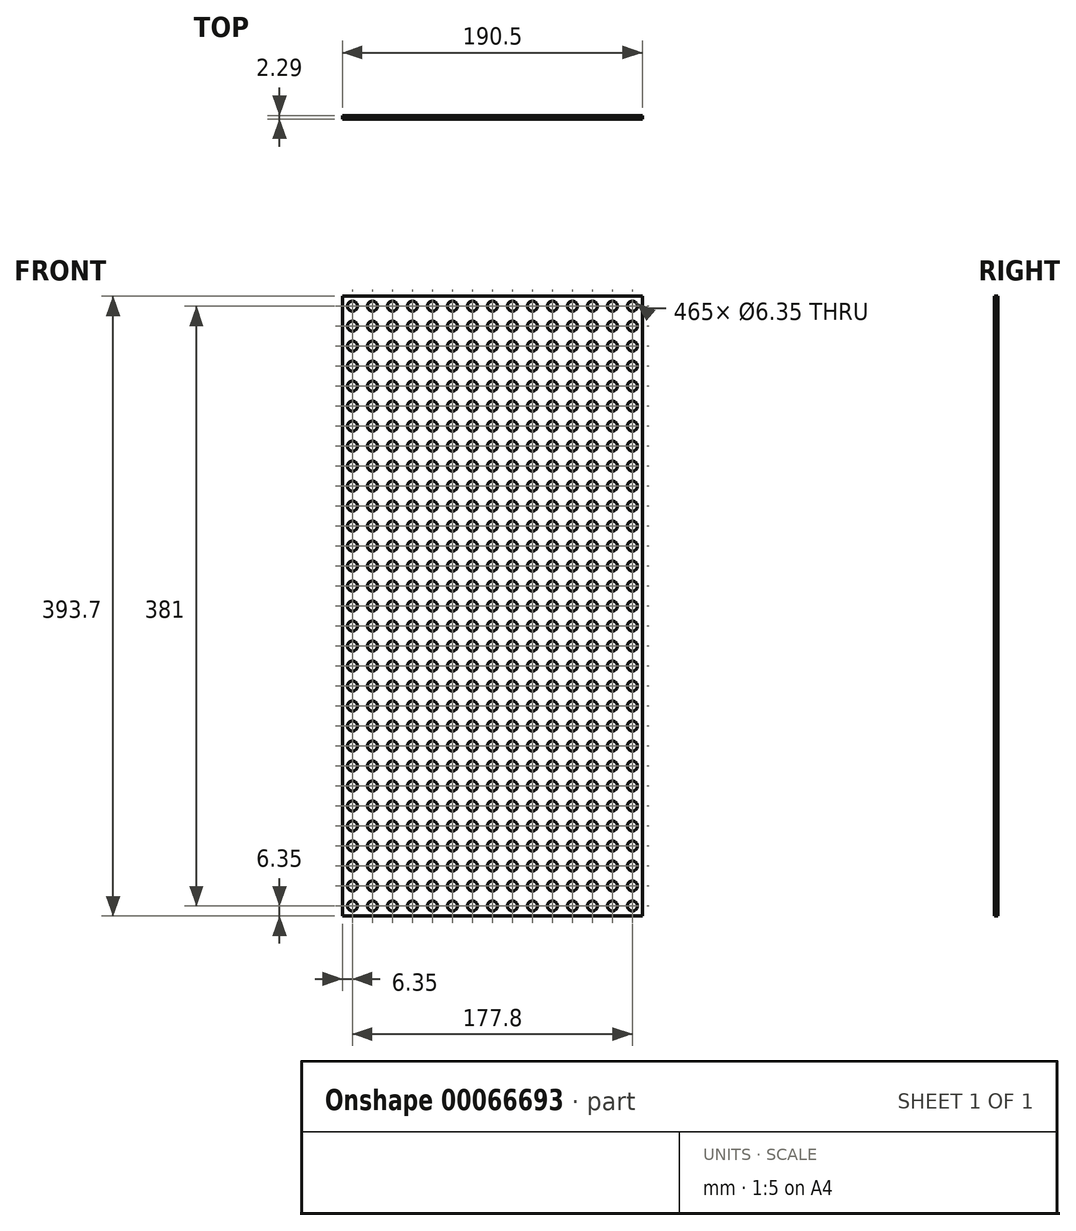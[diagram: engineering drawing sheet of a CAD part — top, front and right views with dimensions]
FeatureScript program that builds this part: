
annotation { "Feature Type Name" : "Feature", "Feature Type Description" : "" }
export const myFeature = defineFeature(function(context is Context, id is Id, definition is map)
    precondition{}
    {
        {
            var Q0;
            Q0=qCreatedBy(makeId("Front.planeOp"),FACE);
            var sketch = newSketch(context, id + "F0", { "sketchPlane" : qUnion([Q0])});
            skLineSegment(sketch, "E0.bottom", {"start": v(-95.25, 196.85) * mm, "end": v(95.25, 196.85) * mm});
            skLineSegment(sketch, "E0.top", {"start": v(-95.25, -196.85) * mm, "end": v(95.25, -196.85) * mm});
            skLineSegment(sketch, "E0.left", {"start": v(-95.25, 196.85) * mm, "end": v(-95.25, -196.85) * mm});
            skLineSegment(sketch, "E0.right", {"start": v(95.25, 196.85) * mm, "end": v(95.25, -196.85) * mm});
            skSolve(sketch);
        }
        {
            var Q0;
            Q0 = qSketchRegion(id + "F0", true);
            extrude(context, id + "F1", {"entities" : qUnion([Q0]), "depth" : 2.3 * mm});
        }
        {
            var Q0;
            Q0=makeQuery(id+"F1.opExtrude","CAP_FACE",FACE,{"disambiguationData":[OSD([sQuery(id+"F0.wireOp",EDGE,"E0.bottom"),sQuery(id+"F0.wireOp",EDGE,"E0.top"),sQuery(id+"F0.wireOp",EDGE,"E0.left"),sQuery(id+"F0.wireOp",EDGE,"E0.right")])],"isStart":false});
            var sketch = newSketch(context, id + "F2", { "sketchPlane" : qUnion([Q0])});
            skCircle(sketch, "E1", {"center": v(-88.9, 190.5) * mm, "radius": 3.18 * mm});
            skCircle(sketch, "E2.0.1.0", {"center": v(-88.9, 177.8) * mm, "radius": 3.18 * mm});
            skCircle(sketch, "E2.1.0.0", {"center": v(-76.2, 190.5) * mm, "radius": 3.18 * mm});
            skCircle(sketch, "E2.1.1.0", {"center": v(-76.2, 177.8) * mm, "radius": 3.18 * mm});
            skCircle(sketch, "E2.2.0.0", {"center": v(-63.5, 190.5) * mm, "radius": 3.18 * mm});
            skCircle(sketch, "E2.2.1.0", {"center": v(-63.5, 177.8) * mm, "radius": 3.18 * mm});
            skLineSegment(sketch, "E2.direction1", {"start": v(-88.9, 190.5) * mm, "end": v(-76.2, 190.5) * mm, "construction": true});
            skLineSegment(sketch, "E2.direction2", {"start": v(-88.9, 190.5) * mm, "end": v(-88.9, 177.8) * mm, "construction": true});
            skCircle(sketch, "E3.0.3.0", {"center": v(-50.8, 190.5) * mm, "radius": 3.18 * mm});
            skCircle(sketch, "E3.0.3.1", {"center": v(-50.8, 177.8) * mm, "radius": 3.18 * mm});
            skCircle(sketch, "E3.0.4.0", {"center": v(-38.1, 190.5) * mm, "radius": 3.18 * mm});
            skCircle(sketch, "E3.0.4.1", {"center": v(-38.1, 177.8) * mm, "radius": 3.18 * mm});
            skCircle(sketch, "E3.0.5.0", {"center": v(-25.4, 190.5) * mm, "radius": 3.18 * mm});
            skCircle(sketch, "E3.0.5.1", {"center": v(-25.4, 177.8) * mm, "radius": 3.18 * mm});
            skCircle(sketch, "E3.0.6.0", {"center": v(-12.7, 190.5) * mm, "radius": 3.18 * mm});
            skCircle(sketch, "E3.0.6.1", {"center": v(-12.7, 177.8) * mm, "radius": 3.18 * mm});
            skCircle(sketch, "E3.0.7.0", {"center": v(0, 190.5) * mm, "radius": 3.18 * mm});
            skCircle(sketch, "E3.0.7.1", {"center": v(0, 177.8) * mm, "radius": 3.18 * mm});
            skCircle(sketch, "E3.0.8.0", {"center": v(12.7, 190.5) * mm, "radius": 3.18 * mm});
            skCircle(sketch, "E3.0.8.1", {"center": v(12.7, 177.8) * mm, "radius": 3.18 * mm});
            skCircle(sketch, "E3.0.9.0", {"center": v(25.4, 190.5) * mm, "radius": 3.18 * mm});
            skCircle(sketch, "E3.0.9.1", {"center": v(25.4, 177.8) * mm, "radius": 3.18 * mm});
            skCircle(sketch, "E3.0.10.0", {"center": v(38.1, 190.5) * mm, "radius": 3.18 * mm});
            skCircle(sketch, "E3.0.10.1", {"center": v(38.1, 177.8) * mm, "radius": 3.18 * mm});
            skCircle(sketch, "E3.0.11.0", {"center": v(50.8, 190.5) * mm, "radius": 3.18 * mm});
            skCircle(sketch, "E3.0.11.1", {"center": v(50.8, 177.8) * mm, "radius": 3.18 * mm});
            skCircle(sketch, "E3.0.12.0", {"center": v(63.5, 190.5) * mm, "radius": 3.18 * mm});
            skCircle(sketch, "E3.0.12.1", {"center": v(63.5, 177.8) * mm, "radius": 3.18 * mm});
            skCircle(sketch, "E3.0.13.0", {"center": v(76.2, 190.5) * mm, "radius": 3.18 * mm});
            skCircle(sketch, "E3.0.13.1", {"center": v(76.2, 177.8) * mm, "radius": 3.18 * mm});
            skCircle(sketch, "E4.0.0.2", {"center": v(-88.9, 165.1) * mm, "radius": 3.18 * mm});
            skCircle(sketch, "E4.0.0.3", {"center": v(-88.9, 152.4) * mm, "radius": 3.18 * mm});
            skCircle(sketch, "E4.0.0.4", {"center": v(-88.9, 139.7) * mm, "radius": 3.18 * mm});
            skCircle(sketch, "E4.0.0.5", {"center": v(-88.9, 127) * mm, "radius": 3.18 * mm});
            skCircle(sketch, "E4.0.0.6", {"center": v(-88.9, 114.3) * mm, "radius": 3.18 * mm});
            skCircle(sketch, "E4.0.0.7", {"center": v(-88.9, 101.6) * mm, "radius": 3.18 * mm});
            skCircle(sketch, "E4.0.0.8", {"center": v(-88.9, 88.9) * mm, "radius": 3.18 * mm});
            skCircle(sketch, "E4.0.0.9", {"center": v(-88.9, 76.2) * mm, "radius": 3.18 * mm});
            skCircle(sketch, "E4.0.0.10", {"center": v(-88.9, 63.5) * mm, "radius": 3.18 * mm});
            skCircle(sketch, "E4.0.0.11", {"center": v(-88.9, 50.8) * mm, "radius": 3.18 * mm});
            skCircle(sketch, "E4.0.0.12", {"center": v(-88.9, 38.1) * mm, "radius": 3.18 * mm});
            skCircle(sketch, "E4.0.0.13", {"center": v(-88.9, 25.4) * mm, "radius": 3.18 * mm});
            skCircle(sketch, "E4.0.0.14", {"center": v(-88.9, 12.7) * mm, "radius": 3.18 * mm});
            skCircle(sketch, "E4.0.0.15", {"center": v(-88.9, 0) * mm, "radius": 3.18 * mm});
            skCircle(sketch, "E4.0.0.16", {"center": v(-88.9, -12.7) * mm, "radius": 3.18 * mm});
            skCircle(sketch, "E4.0.0.17", {"center": v(-88.9, -25.4) * mm, "radius": 3.18 * mm});
            skCircle(sketch, "E4.0.0.18", {"center": v(-88.9, -38.1) * mm, "radius": 3.18 * mm});
            skCircle(sketch, "E4.0.0.19", {"center": v(-88.9, -50.8) * mm, "radius": 3.18 * mm});
            skCircle(sketch, "E4.0.0.20", {"center": v(-88.9, -63.5) * mm, "radius": 3.18 * mm});
            skCircle(sketch, "E4.0.0.21", {"center": v(-88.9, -76.2) * mm, "radius": 3.18 * mm});
            skCircle(sketch, "E4.0.0.22", {"center": v(-88.9, -88.9) * mm, "radius": 3.18 * mm});
            skCircle(sketch, "E4.0.0.23", {"center": v(-88.9, -101.6) * mm, "radius": 3.18 * mm});
            skCircle(sketch, "E4.0.0.24", {"center": v(-88.9, -114.3) * mm, "radius": 3.18 * mm});
            skCircle(sketch, "E4.0.0.25", {"center": v(-88.9, -127) * mm, "radius": 3.18 * mm});
            skCircle(sketch, "E4.0.0.26", {"center": v(-88.9, -139.7) * mm, "radius": 3.18 * mm});
            skCircle(sketch, "E4.0.0.27", {"center": v(-88.9, -152.4) * mm, "radius": 3.18 * mm});
            skCircle(sketch, "E4.0.0.28", {"center": v(-88.9, -165.1) * mm, "radius": 3.18 * mm});
            skCircle(sketch, "E4.0.0.29", {"center": v(-88.9, -177.8) * mm, "radius": 3.18 * mm});
            skCircle(sketch, "E4.0.1.2", {"center": v(-76.2, 165.1) * mm, "radius": 3.18 * mm});
            skCircle(sketch, "E4.0.1.3", {"center": v(-76.2, 152.4) * mm, "radius": 3.18 * mm});
            skCircle(sketch, "E4.0.1.4", {"center": v(-76.2, 139.7) * mm, "radius": 3.18 * mm});
            skCircle(sketch, "E4.0.1.5", {"center": v(-76.2, 127) * mm, "radius": 3.18 * mm});
            skCircle(sketch, "E4.0.1.6", {"center": v(-76.2, 114.3) * mm, "radius": 3.18 * mm});
            skCircle(sketch, "E4.0.1.7", {"center": v(-76.2, 101.6) * mm, "radius": 3.18 * mm});
            skCircle(sketch, "E4.0.1.8", {"center": v(-76.2, 88.9) * mm, "radius": 3.18 * mm});
            skCircle(sketch, "E4.0.1.9", {"center": v(-76.2, 76.2) * mm, "radius": 3.18 * mm});
            skCircle(sketch, "E4.0.1.10", {"center": v(-76.2, 63.5) * mm, "radius": 3.18 * mm});
            skCircle(sketch, "E4.0.1.11", {"center": v(-76.2, 50.8) * mm, "radius": 3.18 * mm});
            skCircle(sketch, "E4.0.1.12", {"center": v(-76.2, 38.1) * mm, "radius": 3.18 * mm});
            skCircle(sketch, "E4.0.1.13", {"center": v(-76.2, 25.4) * mm, "radius": 3.18 * mm});
            skCircle(sketch, "E4.0.1.14", {"center": v(-76.2, 12.7) * mm, "radius": 3.18 * mm});
            skCircle(sketch, "E4.0.1.15", {"center": v(-76.2, 0) * mm, "radius": 3.18 * mm});
            skCircle(sketch, "E4.0.1.16", {"center": v(-76.2, -12.7) * mm, "radius": 3.18 * mm});
            skCircle(sketch, "E4.0.1.17", {"center": v(-76.2, -25.4) * mm, "radius": 3.18 * mm});
            skCircle(sketch, "E4.0.1.18", {"center": v(-76.2, -38.1) * mm, "radius": 3.18 * mm});
            skCircle(sketch, "E4.0.1.19", {"center": v(-76.2, -50.8) * mm, "radius": 3.18 * mm});
            skCircle(sketch, "E4.0.1.20", {"center": v(-76.2, -63.5) * mm, "radius": 3.18 * mm});
            skCircle(sketch, "E4.0.1.21", {"center": v(-76.2, -76.2) * mm, "radius": 3.18 * mm});
            skCircle(sketch, "E4.0.1.22", {"center": v(-76.2, -88.9) * mm, "radius": 3.18 * mm});
            skCircle(sketch, "E4.0.1.23", {"center": v(-76.2, -101.6) * mm, "radius": 3.18 * mm});
            skCircle(sketch, "E4.0.1.24", {"center": v(-76.2, -114.3) * mm, "radius": 3.18 * mm});
            skCircle(sketch, "E4.0.1.25", {"center": v(-76.2, -127) * mm, "radius": 3.18 * mm});
            skCircle(sketch, "E4.0.1.26", {"center": v(-76.2, -139.7) * mm, "radius": 3.18 * mm});
            skCircle(sketch, "E4.0.1.27", {"center": v(-76.2, -152.4) * mm, "radius": 3.18 * mm});
            skCircle(sketch, "E4.0.1.28", {"center": v(-76.2, -165.1) * mm, "radius": 3.18 * mm});
            skCircle(sketch, "E4.0.1.29", {"center": v(-76.2, -177.8) * mm, "radius": 3.18 * mm});
            skCircle(sketch, "E4.0.2.2", {"center": v(-63.5, 165.1) * mm, "radius": 3.18 * mm});
            skCircle(sketch, "E4.0.2.3", {"center": v(-63.5, 152.4) * mm, "radius": 3.18 * mm});
            skCircle(sketch, "E4.0.2.4", {"center": v(-63.5, 139.7) * mm, "radius": 3.18 * mm});
            skCircle(sketch, "E4.0.2.5", {"center": v(-63.5, 127) * mm, "radius": 3.18 * mm});
            skCircle(sketch, "E4.0.2.6", {"center": v(-63.5, 114.3) * mm, "radius": 3.18 * mm});
            skCircle(sketch, "E4.0.2.7", {"center": v(-63.5, 101.6) * mm, "radius": 3.18 * mm});
            skCircle(sketch, "E4.0.2.8", {"center": v(-63.5, 88.9) * mm, "radius": 3.18 * mm});
            skCircle(sketch, "E4.0.2.9", {"center": v(-63.5, 76.2) * mm, "radius": 3.18 * mm});
            skCircle(sketch, "E4.0.2.10", {"center": v(-63.5, 63.5) * mm, "radius": 3.18 * mm});
            skCircle(sketch, "E4.0.2.11", {"center": v(-63.5, 50.8) * mm, "radius": 3.18 * mm});
            skCircle(sketch, "E4.0.2.12", {"center": v(-63.5, 38.1) * mm, "radius": 3.18 * mm});
            skCircle(sketch, "E4.0.2.13", {"center": v(-63.5, 25.4) * mm, "radius": 3.18 * mm});
            skCircle(sketch, "E4.0.2.14", {"center": v(-63.5, 12.7) * mm, "radius": 3.18 * mm});
            skCircle(sketch, "E4.0.2.15", {"center": v(-63.5, 0) * mm, "radius": 3.18 * mm});
            skCircle(sketch, "E4.0.2.16", {"center": v(-63.5, -12.7) * mm, "radius": 3.18 * mm});
            skCircle(sketch, "E4.0.2.17", {"center": v(-63.5, -25.4) * mm, "radius": 3.18 * mm});
            skCircle(sketch, "E4.0.2.18", {"center": v(-63.5, -38.1) * mm, "radius": 3.18 * mm});
            skCircle(sketch, "E4.0.2.19", {"center": v(-63.5, -50.8) * mm, "radius": 3.18 * mm});
            skCircle(sketch, "E4.0.2.20", {"center": v(-63.5, -63.5) * mm, "radius": 3.18 * mm});
            skCircle(sketch, "E4.0.2.21", {"center": v(-63.5, -76.2) * mm, "radius": 3.18 * mm});
            skCircle(sketch, "E4.0.2.22", {"center": v(-63.5, -88.9) * mm, "radius": 3.18 * mm});
            skCircle(sketch, "E4.0.2.23", {"center": v(-63.5, -101.6) * mm, "radius": 3.18 * mm});
            skCircle(sketch, "E4.0.2.24", {"center": v(-63.5, -114.3) * mm, "radius": 3.18 * mm});
            skCircle(sketch, "E4.0.2.25", {"center": v(-63.5, -127) * mm, "radius": 3.18 * mm});
            skCircle(sketch, "E4.0.2.26", {"center": v(-63.5, -139.7) * mm, "radius": 3.18 * mm});
            skCircle(sketch, "E4.0.2.27", {"center": v(-63.5, -152.4) * mm, "radius": 3.18 * mm});
            skCircle(sketch, "E4.0.2.28", {"center": v(-63.5, -165.1) * mm, "radius": 3.18 * mm});
            skCircle(sketch, "E4.0.2.29", {"center": v(-63.5, -177.8) * mm, "radius": 3.18 * mm});
            skCircle(sketch, "E4.0.3.2", {"center": v(-50.8, 165.1) * mm, "radius": 3.18 * mm});
            skCircle(sketch, "E4.0.3.3", {"center": v(-50.8, 152.4) * mm, "radius": 3.18 * mm});
            skCircle(sketch, "E4.0.3.4", {"center": v(-50.8, 139.7) * mm, "radius": 3.18 * mm});
            skCircle(sketch, "E4.0.3.5", {"center": v(-50.8, 127) * mm, "radius": 3.18 * mm});
            skCircle(sketch, "E4.0.3.6", {"center": v(-50.8, 114.3) * mm, "radius": 3.18 * mm});
            skCircle(sketch, "E4.0.3.7", {"center": v(-50.8, 101.6) * mm, "radius": 3.18 * mm});
            skCircle(sketch, "E4.0.3.8", {"center": v(-50.8, 88.9) * mm, "radius": 3.18 * mm});
            skCircle(sketch, "E4.0.3.9", {"center": v(-50.8, 76.2) * mm, "radius": 3.18 * mm});
            skCircle(sketch, "E4.0.3.10", {"center": v(-50.8, 63.5) * mm, "radius": 3.18 * mm});
            skCircle(sketch, "E4.0.3.11", {"center": v(-50.8, 50.8) * mm, "radius": 3.18 * mm});
            skCircle(sketch, "E4.0.3.12", {"center": v(-50.8, 38.1) * mm, "radius": 3.18 * mm});
            skCircle(sketch, "E4.0.3.13", {"center": v(-50.8, 25.4) * mm, "radius": 3.18 * mm});
            skCircle(sketch, "E4.0.3.14", {"center": v(-50.8, 12.7) * mm, "radius": 3.18 * mm});
            skCircle(sketch, "E4.0.3.15", {"center": v(-50.8, 0) * mm, "radius": 3.18 * mm});
            skCircle(sketch, "E4.0.3.16", {"center": v(-50.8, -12.7) * mm, "radius": 3.18 * mm});
            skCircle(sketch, "E4.0.3.17", {"center": v(-50.8, -25.4) * mm, "radius": 3.18 * mm});
            skCircle(sketch, "E4.0.3.18", {"center": v(-50.8, -38.1) * mm, "radius": 3.18 * mm});
            skCircle(sketch, "E4.0.3.19", {"center": v(-50.8, -50.8) * mm, "radius": 3.18 * mm});
            skCircle(sketch, "E4.0.3.20", {"center": v(-50.8, -63.5) * mm, "radius": 3.18 * mm});
            skCircle(sketch, "E4.0.3.21", {"center": v(-50.8, -76.2) * mm, "radius": 3.18 * mm});
            skCircle(sketch, "E4.0.3.22", {"center": v(-50.8, -88.9) * mm, "radius": 3.18 * mm});
            skCircle(sketch, "E4.0.3.23", {"center": v(-50.8, -101.6) * mm, "radius": 3.18 * mm});
            skCircle(sketch, "E4.0.3.24", {"center": v(-50.8, -114.3) * mm, "radius": 3.18 * mm});
            skCircle(sketch, "E4.0.3.25", {"center": v(-50.8, -127) * mm, "radius": 3.18 * mm});
            skCircle(sketch, "E4.0.3.26", {"center": v(-50.8, -139.7) * mm, "radius": 3.18 * mm});
            skCircle(sketch, "E4.0.3.27", {"center": v(-50.8, -152.4) * mm, "radius": 3.18 * mm});
            skCircle(sketch, "E4.0.3.28", {"center": v(-50.8, -165.1) * mm, "radius": 3.18 * mm});
            skCircle(sketch, "E4.0.3.29", {"center": v(-50.8, -177.8) * mm, "radius": 3.18 * mm});
            skCircle(sketch, "E4.0.4.2", {"center": v(-38.1, 165.1) * mm, "radius": 3.18 * mm});
            skCircle(sketch, "E4.0.4.3", {"center": v(-38.1, 152.4) * mm, "radius": 3.18 * mm});
            skCircle(sketch, "E4.0.4.4", {"center": v(-38.1, 139.7) * mm, "radius": 3.18 * mm});
            skCircle(sketch, "E4.0.4.5", {"center": v(-38.1, 127) * mm, "radius": 3.18 * mm});
            skCircle(sketch, "E4.0.4.6", {"center": v(-38.1, 114.3) * mm, "radius": 3.18 * mm});
            skCircle(sketch, "E4.0.4.7", {"center": v(-38.1, 101.6) * mm, "radius": 3.18 * mm});
            skCircle(sketch, "E4.0.4.8", {"center": v(-38.1, 88.9) * mm, "radius": 3.18 * mm});
            skCircle(sketch, "E4.0.4.9", {"center": v(-38.1, 76.2) * mm, "radius": 3.18 * mm});
            skCircle(sketch, "E4.0.4.10", {"center": v(-38.1, 63.5) * mm, "radius": 3.18 * mm});
            skCircle(sketch, "E4.0.4.11", {"center": v(-38.1, 50.8) * mm, "radius": 3.18 * mm});
            skCircle(sketch, "E4.0.4.12", {"center": v(-38.1, 38.1) * mm, "radius": 3.18 * mm});
            skCircle(sketch, "E4.0.4.13", {"center": v(-38.1, 25.4) * mm, "radius": 3.18 * mm});
            skCircle(sketch, "E4.0.4.14", {"center": v(-38.1, 12.7) * mm, "radius": 3.18 * mm});
            skCircle(sketch, "E4.0.4.15", {"center": v(-38.1, 0) * mm, "radius": 3.18 * mm});
            skCircle(sketch, "E4.0.4.16", {"center": v(-38.1, -12.7) * mm, "radius": 3.18 * mm});
            skCircle(sketch, "E4.0.4.17", {"center": v(-38.1, -25.4) * mm, "radius": 3.18 * mm});
            skCircle(sketch, "E4.0.4.18", {"center": v(-38.1, -38.1) * mm, "radius": 3.18 * mm});
            skCircle(sketch, "E4.0.4.19", {"center": v(-38.1, -50.8) * mm, "radius": 3.18 * mm});
            skCircle(sketch, "E4.0.4.20", {"center": v(-38.1, -63.5) * mm, "radius": 3.18 * mm});
            skCircle(sketch, "E4.0.4.21", {"center": v(-38.1, -76.2) * mm, "radius": 3.18 * mm});
            skCircle(sketch, "E4.0.4.22", {"center": v(-38.1, -88.9) * mm, "radius": 3.18 * mm});
            skCircle(sketch, "E4.0.4.23", {"center": v(-38.1, -101.6) * mm, "radius": 3.18 * mm});
            skCircle(sketch, "E4.0.4.24", {"center": v(-38.1, -114.3) * mm, "radius": 3.18 * mm});
            skCircle(sketch, "E4.0.4.25", {"center": v(-38.1, -127) * mm, "radius": 3.18 * mm});
            skCircle(sketch, "E4.0.4.26", {"center": v(-38.1, -139.7) * mm, "radius": 3.18 * mm});
            skCircle(sketch, "E4.0.4.27", {"center": v(-38.1, -152.4) * mm, "radius": 3.18 * mm});
            skCircle(sketch, "E4.0.4.28", {"center": v(-38.1, -165.1) * mm, "radius": 3.18 * mm});
            skCircle(sketch, "E4.0.4.29", {"center": v(-38.1, -177.8) * mm, "radius": 3.18 * mm});
            skCircle(sketch, "E4.0.5.2", {"center": v(-25.4, 165.1) * mm, "radius": 3.18 * mm});
            skCircle(sketch, "E4.0.5.3", {"center": v(-25.4, 152.4) * mm, "radius": 3.18 * mm});
            skCircle(sketch, "E4.0.5.4", {"center": v(-25.4, 139.7) * mm, "radius": 3.18 * mm});
            skCircle(sketch, "E4.0.5.5", {"center": v(-25.4, 127) * mm, "radius": 3.18 * mm});
            skCircle(sketch, "E4.0.5.6", {"center": v(-25.4, 114.3) * mm, "radius": 3.18 * mm});
            skCircle(sketch, "E4.0.5.7", {"center": v(-25.4, 101.6) * mm, "radius": 3.18 * mm});
            skCircle(sketch, "E4.0.5.8", {"center": v(-25.4, 88.9) * mm, "radius": 3.18 * mm});
            skCircle(sketch, "E4.0.5.9", {"center": v(-25.4, 76.2) * mm, "radius": 3.18 * mm});
            skCircle(sketch, "E4.0.5.10", {"center": v(-25.4, 63.5) * mm, "radius": 3.18 * mm});
            skCircle(sketch, "E4.0.5.11", {"center": v(-25.4, 50.8) * mm, "radius": 3.18 * mm});
            skCircle(sketch, "E4.0.5.12", {"center": v(-25.4, 38.1) * mm, "radius": 3.18 * mm});
            skCircle(sketch, "E4.0.5.13", {"center": v(-25.4, 25.4) * mm, "radius": 3.18 * mm});
            skCircle(sketch, "E4.0.5.14", {"center": v(-25.4, 12.7) * mm, "radius": 3.18 * mm});
            skCircle(sketch, "E4.0.5.15", {"center": v(-25.4, 0) * mm, "radius": 3.18 * mm});
            skCircle(sketch, "E4.0.5.16", {"center": v(-25.4, -12.7) * mm, "radius": 3.18 * mm});
            skCircle(sketch, "E4.0.5.17", {"center": v(-25.4, -25.4) * mm, "radius": 3.18 * mm});
            skCircle(sketch, "E4.0.5.18", {"center": v(-25.4, -38.1) * mm, "radius": 3.18 * mm});
            skCircle(sketch, "E4.0.5.19", {"center": v(-25.4, -50.8) * mm, "radius": 3.18 * mm});
            skCircle(sketch, "E4.0.5.20", {"center": v(-25.4, -63.5) * mm, "radius": 3.18 * mm});
            skCircle(sketch, "E4.0.5.21", {"center": v(-25.4, -76.2) * mm, "radius": 3.18 * mm});
            skCircle(sketch, "E4.0.5.22", {"center": v(-25.4, -88.9) * mm, "radius": 3.18 * mm});
            skCircle(sketch, "E4.0.5.23", {"center": v(-25.4, -101.6) * mm, "radius": 3.18 * mm});
            skCircle(sketch, "E4.0.5.24", {"center": v(-25.4, -114.3) * mm, "radius": 3.18 * mm});
            skCircle(sketch, "E4.0.5.25", {"center": v(-25.4, -127) * mm, "radius": 3.18 * mm});
            skCircle(sketch, "E4.0.5.26", {"center": v(-25.4, -139.7) * mm, "radius": 3.18 * mm});
            skCircle(sketch, "E4.0.5.27", {"center": v(-25.4, -152.4) * mm, "radius": 3.18 * mm});
            skCircle(sketch, "E4.0.5.28", {"center": v(-25.4, -165.1) * mm, "radius": 3.18 * mm});
            skCircle(sketch, "E4.0.5.29", {"center": v(-25.4, -177.8) * mm, "radius": 3.18 * mm});
            skCircle(sketch, "E4.0.6.2", {"center": v(-12.7, 165.1) * mm, "radius": 3.18 * mm});
            skCircle(sketch, "E4.0.6.3", {"center": v(-12.7, 152.4) * mm, "radius": 3.18 * mm});
            skCircle(sketch, "E4.0.6.4", {"center": v(-12.7, 139.7) * mm, "radius": 3.18 * mm});
            skCircle(sketch, "E4.0.6.5", {"center": v(-12.7, 127) * mm, "radius": 3.18 * mm});
            skCircle(sketch, "E4.0.6.6", {"center": v(-12.7, 114.3) * mm, "radius": 3.18 * mm});
            skCircle(sketch, "E4.0.6.7", {"center": v(-12.7, 101.6) * mm, "radius": 3.18 * mm});
            skCircle(sketch, "E4.0.6.8", {"center": v(-12.7, 88.9) * mm, "radius": 3.18 * mm});
            skCircle(sketch, "E4.0.6.9", {"center": v(-12.7, 76.2) * mm, "radius": 3.18 * mm});
            skCircle(sketch, "E4.0.6.10", {"center": v(-12.7, 63.5) * mm, "radius": 3.18 * mm});
            skCircle(sketch, "E4.0.6.11", {"center": v(-12.7, 50.8) * mm, "radius": 3.18 * mm});
            skCircle(sketch, "E4.0.6.12", {"center": v(-12.7, 38.1) * mm, "radius": 3.18 * mm});
            skCircle(sketch, "E4.0.6.13", {"center": v(-12.7, 25.4) * mm, "radius": 3.18 * mm});
            skCircle(sketch, "E4.0.6.14", {"center": v(-12.7, 12.7) * mm, "radius": 3.18 * mm});
            skCircle(sketch, "E4.0.6.15", {"center": v(-12.7, 0) * mm, "radius": 3.18 * mm});
            skCircle(sketch, "E4.0.6.16", {"center": v(-12.7, -12.7) * mm, "radius": 3.18 * mm});
            skCircle(sketch, "E4.0.6.17", {"center": v(-12.7, -25.4) * mm, "radius": 3.18 * mm});
            skCircle(sketch, "E4.0.6.18", {"center": v(-12.7, -38.1) * mm, "radius": 3.18 * mm});
            skCircle(sketch, "E4.0.6.19", {"center": v(-12.7, -50.8) * mm, "radius": 3.18 * mm});
            skCircle(sketch, "E4.0.6.20", {"center": v(-12.7, -63.5) * mm, "radius": 3.18 * mm});
            skCircle(sketch, "E4.0.6.21", {"center": v(-12.7, -76.2) * mm, "radius": 3.18 * mm});
            skCircle(sketch, "E4.0.6.22", {"center": v(-12.7, -88.9) * mm, "radius": 3.18 * mm});
            skCircle(sketch, "E4.0.6.23", {"center": v(-12.7, -101.6) * mm, "radius": 3.18 * mm});
            skCircle(sketch, "E4.0.6.24", {"center": v(-12.7, -114.3) * mm, "radius": 3.18 * mm});
            skCircle(sketch, "E4.0.6.25", {"center": v(-12.7, -127) * mm, "radius": 3.18 * mm});
            skCircle(sketch, "E4.0.6.26", {"center": v(-12.7, -139.7) * mm, "radius": 3.18 * mm});
            skCircle(sketch, "E4.0.6.27", {"center": v(-12.7, -152.4) * mm, "radius": 3.18 * mm});
            skCircle(sketch, "E4.0.6.28", {"center": v(-12.7, -165.1) * mm, "radius": 3.18 * mm});
            skCircle(sketch, "E4.0.6.29", {"center": v(-12.7, -177.8) * mm, "radius": 3.18 * mm});
            skCircle(sketch, "E4.0.7.2", {"center": v(0, 165.1) * mm, "radius": 3.18 * mm});
            skCircle(sketch, "E4.0.7.3", {"center": v(0, 152.4) * mm, "radius": 3.18 * mm});
            skCircle(sketch, "E4.0.7.4", {"center": v(0, 139.7) * mm, "radius": 3.18 * mm});
            skCircle(sketch, "E4.0.7.5", {"center": v(0, 127) * mm, "radius": 3.18 * mm});
            skCircle(sketch, "E4.0.7.6", {"center": v(0, 114.3) * mm, "radius": 3.18 * mm});
            skCircle(sketch, "E4.0.7.7", {"center": v(0, 101.6) * mm, "radius": 3.18 * mm});
            skCircle(sketch, "E4.0.7.8", {"center": v(0, 88.9) * mm, "radius": 3.18 * mm});
            skCircle(sketch, "E4.0.7.9", {"center": v(0, 76.2) * mm, "radius": 3.18 * mm});
            skCircle(sketch, "E4.0.7.10", {"center": v(0, 63.5) * mm, "radius": 3.18 * mm});
            skCircle(sketch, "E4.0.7.11", {"center": v(0, 50.8) * mm, "radius": 3.18 * mm});
            skCircle(sketch, "E4.0.7.12", {"center": v(0, 38.1) * mm, "radius": 3.18 * mm});
            skCircle(sketch, "E4.0.7.13", {"center": v(0, 25.4) * mm, "radius": 3.18 * mm});
            skCircle(sketch, "E4.0.7.14", {"center": v(0, 12.7) * mm, "radius": 3.18 * mm});
            skCircle(sketch, "E4.0.7.15", {"center": v(0, 0) * mm, "radius": 3.18 * mm});
            skCircle(sketch, "E4.0.7.16", {"center": v(0, -12.7) * mm, "radius": 3.18 * mm});
            skCircle(sketch, "E4.0.7.17", {"center": v(0, -25.4) * mm, "radius": 3.18 * mm});
            skCircle(sketch, "E4.0.7.18", {"center": v(0, -38.1) * mm, "radius": 3.18 * mm});
            skCircle(sketch, "E4.0.7.19", {"center": v(0, -50.8) * mm, "radius": 3.18 * mm});
            skCircle(sketch, "E4.0.7.20", {"center": v(0, -63.5) * mm, "radius": 3.18 * mm});
            skCircle(sketch, "E4.0.7.21", {"center": v(0, -76.2) * mm, "radius": 3.18 * mm});
            skCircle(sketch, "E4.0.7.22", {"center": v(0, -88.9) * mm, "radius": 3.18 * mm});
            skCircle(sketch, "E4.0.7.23", {"center": v(0, -101.6) * mm, "radius": 3.18 * mm});
            skCircle(sketch, "E4.0.7.24", {"center": v(0, -114.3) * mm, "radius": 3.18 * mm});
            skCircle(sketch, "E4.0.7.25", {"center": v(0, -127) * mm, "radius": 3.18 * mm});
            skCircle(sketch, "E4.0.7.26", {"center": v(0, -139.7) * mm, "radius": 3.18 * mm});
            skCircle(sketch, "E4.0.7.27", {"center": v(0, -152.4) * mm, "radius": 3.18 * mm});
            skCircle(sketch, "E4.0.7.28", {"center": v(0, -165.1) * mm, "radius": 3.18 * mm});
            skCircle(sketch, "E4.0.7.29", {"center": v(0, -177.8) * mm, "radius": 3.18 * mm});
            skCircle(sketch, "E4.0.8.2", {"center": v(12.7, 165.1) * mm, "radius": 3.18 * mm});
            skCircle(sketch, "E4.0.8.3", {"center": v(12.7, 152.4) * mm, "radius": 3.18 * mm});
            skCircle(sketch, "E4.0.8.4", {"center": v(12.7, 139.7) * mm, "radius": 3.18 * mm});
            skCircle(sketch, "E4.0.8.5", {"center": v(12.7, 127) * mm, "radius": 3.18 * mm});
            skCircle(sketch, "E4.0.8.6", {"center": v(12.7, 114.3) * mm, "radius": 3.18 * mm});
            skCircle(sketch, "E4.0.8.7", {"center": v(12.7, 101.6) * mm, "radius": 3.18 * mm});
            skCircle(sketch, "E4.0.8.8", {"center": v(12.7, 88.9) * mm, "radius": 3.18 * mm});
            skCircle(sketch, "E4.0.8.9", {"center": v(12.7, 76.2) * mm, "radius": 3.18 * mm});
            skCircle(sketch, "E4.0.8.10", {"center": v(12.7, 63.5) * mm, "radius": 3.18 * mm});
            skCircle(sketch, "E4.0.8.11", {"center": v(12.7, 50.8) * mm, "radius": 3.18 * mm});
            skCircle(sketch, "E4.0.8.12", {"center": v(12.7, 38.1) * mm, "radius": 3.18 * mm});
            skCircle(sketch, "E4.0.8.13", {"center": v(12.7, 25.4) * mm, "radius": 3.18 * mm});
            skCircle(sketch, "E4.0.8.14", {"center": v(12.7, 12.7) * mm, "radius": 3.18 * mm});
            skCircle(sketch, "E4.0.8.15", {"center": v(12.7, 0) * mm, "radius": 3.18 * mm});
            skCircle(sketch, "E4.0.8.16", {"center": v(12.7, -12.7) * mm, "radius": 3.18 * mm});
            skCircle(sketch, "E4.0.8.17", {"center": v(12.7, -25.4) * mm, "radius": 3.18 * mm});
            skCircle(sketch, "E4.0.8.18", {"center": v(12.7, -38.1) * mm, "radius": 3.18 * mm});
            skCircle(sketch, "E4.0.8.19", {"center": v(12.7, -50.8) * mm, "radius": 3.18 * mm});
            skCircle(sketch, "E4.0.8.20", {"center": v(12.7, -63.5) * mm, "radius": 3.18 * mm});
            skCircle(sketch, "E4.0.8.21", {"center": v(12.7, -76.2) * mm, "radius": 3.18 * mm});
            skCircle(sketch, "E4.0.8.22", {"center": v(12.7, -88.9) * mm, "radius": 3.18 * mm});
            skCircle(sketch, "E4.0.8.23", {"center": v(12.7, -101.6) * mm, "radius": 3.18 * mm});
            skCircle(sketch, "E4.0.8.24", {"center": v(12.7, -114.3) * mm, "radius": 3.18 * mm});
            skCircle(sketch, "E4.0.8.25", {"center": v(12.7, -127) * mm, "radius": 3.18 * mm});
            skCircle(sketch, "E4.0.8.26", {"center": v(12.7, -139.7) * mm, "radius": 3.18 * mm});
            skCircle(sketch, "E4.0.8.27", {"center": v(12.7, -152.4) * mm, "radius": 3.18 * mm});
            skCircle(sketch, "E4.0.8.28", {"center": v(12.7, -165.1) * mm, "radius": 3.18 * mm});
            skCircle(sketch, "E4.0.8.29", {"center": v(12.7, -177.8) * mm, "radius": 3.18 * mm});
            skCircle(sketch, "E4.0.9.2", {"center": v(25.4, 165.1) * mm, "radius": 3.18 * mm});
            skCircle(sketch, "E4.0.9.3", {"center": v(25.4, 152.4) * mm, "radius": 3.18 * mm});
            skCircle(sketch, "E4.0.9.4", {"center": v(25.4, 139.7) * mm, "radius": 3.18 * mm});
            skCircle(sketch, "E4.0.9.5", {"center": v(25.4, 127) * mm, "radius": 3.18 * mm});
            skCircle(sketch, "E4.0.9.6", {"center": v(25.4, 114.3) * mm, "radius": 3.18 * mm});
            skCircle(sketch, "E4.0.9.7", {"center": v(25.4, 101.6) * mm, "radius": 3.18 * mm});
            skCircle(sketch, "E4.0.9.8", {"center": v(25.4, 88.9) * mm, "radius": 3.18 * mm});
            skCircle(sketch, "E4.0.9.9", {"center": v(25.4, 76.2) * mm, "radius": 3.18 * mm});
            skCircle(sketch, "E4.0.9.10", {"center": v(25.4, 63.5) * mm, "radius": 3.18 * mm});
            skCircle(sketch, "E4.0.9.11", {"center": v(25.4, 50.8) * mm, "radius": 3.18 * mm});
            skCircle(sketch, "E4.0.9.12", {"center": v(25.4, 38.1) * mm, "radius": 3.18 * mm});
            skCircle(sketch, "E4.0.9.13", {"center": v(25.4, 25.4) * mm, "radius": 3.18 * mm});
            skCircle(sketch, "E4.0.9.14", {"center": v(25.4, 12.7) * mm, "radius": 3.18 * mm});
            skCircle(sketch, "E4.0.9.15", {"center": v(25.4, 0) * mm, "radius": 3.18 * mm});
            skCircle(sketch, "E4.0.9.16", {"center": v(25.4, -12.7) * mm, "radius": 3.18 * mm});
            skCircle(sketch, "E4.0.9.17", {"center": v(25.4, -25.4) * mm, "radius": 3.18 * mm});
            skCircle(sketch, "E4.0.9.18", {"center": v(25.4, -38.1) * mm, "radius": 3.18 * mm});
            skCircle(sketch, "E4.0.9.19", {"center": v(25.4, -50.8) * mm, "radius": 3.18 * mm});
            skCircle(sketch, "E4.0.9.20", {"center": v(25.4, -63.5) * mm, "radius": 3.18 * mm});
            skCircle(sketch, "E4.0.9.21", {"center": v(25.4, -76.2) * mm, "radius": 3.18 * mm});
            skCircle(sketch, "E4.0.9.22", {"center": v(25.4, -88.9) * mm, "radius": 3.18 * mm});
            skCircle(sketch, "E4.0.9.23", {"center": v(25.4, -101.6) * mm, "radius": 3.18 * mm});
            skCircle(sketch, "E4.0.9.24", {"center": v(25.4, -114.3) * mm, "radius": 3.18 * mm});
            skCircle(sketch, "E4.0.9.25", {"center": v(25.4, -127) * mm, "radius": 3.18 * mm});
            skCircle(sketch, "E4.0.9.26", {"center": v(25.4, -139.7) * mm, "radius": 3.18 * mm});
            skCircle(sketch, "E4.0.9.27", {"center": v(25.4, -152.4) * mm, "radius": 3.18 * mm});
            skCircle(sketch, "E4.0.9.28", {"center": v(25.4, -165.1) * mm, "radius": 3.18 * mm});
            skCircle(sketch, "E4.0.9.29", {"center": v(25.4, -177.8) * mm, "radius": 3.18 * mm});
            skCircle(sketch, "E4.0.10.2", {"center": v(38.1, 165.1) * mm, "radius": 3.18 * mm});
            skCircle(sketch, "E4.0.10.3", {"center": v(38.1, 152.4) * mm, "radius": 3.18 * mm});
            skCircle(sketch, "E4.0.10.4", {"center": v(38.1, 139.7) * mm, "radius": 3.18 * mm});
            skCircle(sketch, "E4.0.10.5", {"center": v(38.1, 127) * mm, "radius": 3.18 * mm});
            skCircle(sketch, "E4.0.10.6", {"center": v(38.1, 114.3) * mm, "radius": 3.18 * mm});
            skCircle(sketch, "E4.0.10.7", {"center": v(38.1, 101.6) * mm, "radius": 3.18 * mm});
            skCircle(sketch, "E4.0.10.8", {"center": v(38.1, 88.9) * mm, "radius": 3.18 * mm});
            skCircle(sketch, "E4.0.10.9", {"center": v(38.1, 76.2) * mm, "radius": 3.18 * mm});
            skCircle(sketch, "E4.0.10.10", {"center": v(38.1, 63.5) * mm, "radius": 3.18 * mm});
            skCircle(sketch, "E4.0.10.11", {"center": v(38.1, 50.8) * mm, "radius": 3.18 * mm});
            skCircle(sketch, "E4.0.10.12", {"center": v(38.1, 38.1) * mm, "radius": 3.18 * mm});
            skCircle(sketch, "E4.0.10.13", {"center": v(38.1, 25.4) * mm, "radius": 3.18 * mm});
            skCircle(sketch, "E4.0.10.14", {"center": v(38.1, 12.7) * mm, "radius": 3.18 * mm});
            skCircle(sketch, "E4.0.10.15", {"center": v(38.1, 0) * mm, "radius": 3.18 * mm});
            skCircle(sketch, "E4.0.10.16", {"center": v(38.1, -12.7) * mm, "radius": 3.18 * mm});
            skCircle(sketch, "E4.0.10.17", {"center": v(38.1, -25.4) * mm, "radius": 3.18 * mm});
            skCircle(sketch, "E4.0.10.18", {"center": v(38.1, -38.1) * mm, "radius": 3.18 * mm});
            skCircle(sketch, "E4.0.10.19", {"center": v(38.1, -50.8) * mm, "radius": 3.18 * mm});
            skCircle(sketch, "E4.0.10.20", {"center": v(38.1, -63.5) * mm, "radius": 3.18 * mm});
            skCircle(sketch, "E4.0.10.21", {"center": v(38.1, -76.2) * mm, "radius": 3.18 * mm});
            skCircle(sketch, "E4.0.10.22", {"center": v(38.1, -88.9) * mm, "radius": 3.18 * mm});
            skCircle(sketch, "E4.0.10.23", {"center": v(38.1, -101.6) * mm, "radius": 3.18 * mm});
            skCircle(sketch, "E4.0.10.24", {"center": v(38.1, -114.3) * mm, "radius": 3.18 * mm});
            skCircle(sketch, "E4.0.10.25", {"center": v(38.1, -127) * mm, "radius": 3.18 * mm});
            skCircle(sketch, "E4.0.10.26", {"center": v(38.1, -139.7) * mm, "radius": 3.18 * mm});
            skCircle(sketch, "E4.0.10.27", {"center": v(38.1, -152.4) * mm, "radius": 3.18 * mm});
            skCircle(sketch, "E4.0.10.28", {"center": v(38.1, -165.1) * mm, "radius": 3.18 * mm});
            skCircle(sketch, "E4.0.10.29", {"center": v(38.1, -177.8) * mm, "radius": 3.18 * mm});
            skCircle(sketch, "E4.0.11.2", {"center": v(50.8, 165.1) * mm, "radius": 3.18 * mm});
            skCircle(sketch, "E4.0.11.3", {"center": v(50.8, 152.4) * mm, "radius": 3.18 * mm});
            skCircle(sketch, "E4.0.11.4", {"center": v(50.8, 139.7) * mm, "radius": 3.18 * mm});
            skCircle(sketch, "E4.0.11.5", {"center": v(50.8, 127) * mm, "radius": 3.18 * mm});
            skCircle(sketch, "E4.0.11.6", {"center": v(50.8, 114.3) * mm, "radius": 3.18 * mm});
            skCircle(sketch, "E4.0.11.7", {"center": v(50.8, 101.6) * mm, "radius": 3.18 * mm});
            skCircle(sketch, "E4.0.11.8", {"center": v(50.8, 88.9) * mm, "radius": 3.18 * mm});
            skCircle(sketch, "E4.0.11.9", {"center": v(50.8, 76.2) * mm, "radius": 3.18 * mm});
            skCircle(sketch, "E4.0.11.10", {"center": v(50.8, 63.5) * mm, "radius": 3.18 * mm});
            skCircle(sketch, "E4.0.11.11", {"center": v(50.8, 50.8) * mm, "radius": 3.18 * mm});
            skCircle(sketch, "E4.0.11.12", {"center": v(50.8, 38.1) * mm, "radius": 3.18 * mm});
            skCircle(sketch, "E4.0.11.13", {"center": v(50.8, 25.4) * mm, "radius": 3.18 * mm});
            skCircle(sketch, "E4.0.11.14", {"center": v(50.8, 12.7) * mm, "radius": 3.18 * mm});
            skCircle(sketch, "E4.0.11.15", {"center": v(50.8, 0) * mm, "radius": 3.18 * mm});
            skCircle(sketch, "E4.0.11.16", {"center": v(50.8, -12.7) * mm, "radius": 3.18 * mm});
            skCircle(sketch, "E4.0.11.17", {"center": v(50.8, -25.4) * mm, "radius": 3.18 * mm});
            skCircle(sketch, "E4.0.11.18", {"center": v(50.8, -38.1) * mm, "radius": 3.18 * mm});
            skCircle(sketch, "E4.0.11.19", {"center": v(50.8, -50.8) * mm, "radius": 3.18 * mm});
            skCircle(sketch, "E4.0.11.20", {"center": v(50.8, -63.5) * mm, "radius": 3.18 * mm});
            skCircle(sketch, "E4.0.11.21", {"center": v(50.8, -76.2) * mm, "radius": 3.18 * mm});
            skCircle(sketch, "E4.0.11.22", {"center": v(50.8, -88.9) * mm, "radius": 3.18 * mm});
            skCircle(sketch, "E4.0.11.23", {"center": v(50.8, -101.6) * mm, "radius": 3.18 * mm});
            skCircle(sketch, "E4.0.11.24", {"center": v(50.8, -114.3) * mm, "radius": 3.18 * mm});
            skCircle(sketch, "E4.0.11.25", {"center": v(50.8, -127) * mm, "radius": 3.18 * mm});
            skCircle(sketch, "E4.0.11.26", {"center": v(50.8, -139.7) * mm, "radius": 3.18 * mm});
            skCircle(sketch, "E4.0.11.27", {"center": v(50.8, -152.4) * mm, "radius": 3.18 * mm});
            skCircle(sketch, "E4.0.11.28", {"center": v(50.8, -165.1) * mm, "radius": 3.18 * mm});
            skCircle(sketch, "E4.0.11.29", {"center": v(50.8, -177.8) * mm, "radius": 3.18 * mm});
            skCircle(sketch, "E4.0.12.2", {"center": v(63.5, 165.1) * mm, "radius": 3.18 * mm});
            skCircle(sketch, "E4.0.12.3", {"center": v(63.5, 152.4) * mm, "radius": 3.18 * mm});
            skCircle(sketch, "E4.0.12.4", {"center": v(63.5, 139.7) * mm, "radius": 3.18 * mm});
            skCircle(sketch, "E4.0.12.5", {"center": v(63.5, 127) * mm, "radius": 3.18 * mm});
            skCircle(sketch, "E4.0.12.6", {"center": v(63.5, 114.3) * mm, "radius": 3.18 * mm});
            skCircle(sketch, "E4.0.12.7", {"center": v(63.5, 101.6) * mm, "radius": 3.18 * mm});
            skCircle(sketch, "E4.0.12.8", {"center": v(63.5, 88.9) * mm, "radius": 3.18 * mm});
            skCircle(sketch, "E4.0.12.9", {"center": v(63.5, 76.2) * mm, "radius": 3.18 * mm});
            skCircle(sketch, "E4.0.12.10", {"center": v(63.5, 63.5) * mm, "radius": 3.18 * mm});
            skCircle(sketch, "E4.0.12.11", {"center": v(63.5, 50.8) * mm, "radius": 3.18 * mm});
            skCircle(sketch, "E4.0.12.12", {"center": v(63.5, 38.1) * mm, "radius": 3.18 * mm});
            skCircle(sketch, "E4.0.12.13", {"center": v(63.5, 25.4) * mm, "radius": 3.18 * mm});
            skCircle(sketch, "E4.0.12.14", {"center": v(63.5, 12.7) * mm, "radius": 3.18 * mm});
            skCircle(sketch, "E4.0.12.15", {"center": v(63.5, 0) * mm, "radius": 3.18 * mm});
            skCircle(sketch, "E4.0.12.16", {"center": v(63.5, -12.7) * mm, "radius": 3.18 * mm});
            skCircle(sketch, "E4.0.12.17", {"center": v(63.5, -25.4) * mm, "radius": 3.18 * mm});
            skCircle(sketch, "E4.0.12.18", {"center": v(63.5, -38.1) * mm, "radius": 3.18 * mm});
            skCircle(sketch, "E4.0.12.19", {"center": v(63.5, -50.8) * mm, "radius": 3.18 * mm});
            skCircle(sketch, "E4.0.12.20", {"center": v(63.5, -63.5) * mm, "radius": 3.18 * mm});
            skCircle(sketch, "E4.0.12.21", {"center": v(63.5, -76.2) * mm, "radius": 3.18 * mm});
            skCircle(sketch, "E4.0.12.22", {"center": v(63.5, -88.9) * mm, "radius": 3.18 * mm});
            skCircle(sketch, "E4.0.12.23", {"center": v(63.5, -101.6) * mm, "radius": 3.18 * mm});
            skCircle(sketch, "E4.0.12.24", {"center": v(63.5, -114.3) * mm, "radius": 3.18 * mm});
            skCircle(sketch, "E4.0.12.25", {"center": v(63.5, -127) * mm, "radius": 3.18 * mm});
            skCircle(sketch, "E4.0.12.26", {"center": v(63.5, -139.7) * mm, "radius": 3.18 * mm});
            skCircle(sketch, "E4.0.12.27", {"center": v(63.5, -152.4) * mm, "radius": 3.18 * mm});
            skCircle(sketch, "E4.0.12.28", {"center": v(63.5, -165.1) * mm, "radius": 3.18 * mm});
            skCircle(sketch, "E4.0.12.29", {"center": v(63.5, -177.8) * mm, "radius": 3.18 * mm});
            skCircle(sketch, "E4.0.13.2", {"center": v(76.2, 165.1) * mm, "radius": 3.18 * mm});
            skCircle(sketch, "E4.0.13.3", {"center": v(76.2, 152.4) * mm, "radius": 3.18 * mm});
            skCircle(sketch, "E4.0.13.4", {"center": v(76.2, 139.7) * mm, "radius": 3.18 * mm});
            skCircle(sketch, "E4.0.13.5", {"center": v(76.2, 127) * mm, "radius": 3.18 * mm});
            skCircle(sketch, "E4.0.13.6", {"center": v(76.2, 114.3) * mm, "radius": 3.18 * mm});
            skCircle(sketch, "E4.0.13.7", {"center": v(76.2, 101.6) * mm, "radius": 3.18 * mm});
            skCircle(sketch, "E4.0.13.8", {"center": v(76.2, 88.9) * mm, "radius": 3.18 * mm});
            skCircle(sketch, "E4.0.13.9", {"center": v(76.2, 76.2) * mm, "radius": 3.18 * mm});
            skCircle(sketch, "E4.0.13.10", {"center": v(76.2, 63.5) * mm, "radius": 3.18 * mm});
            skCircle(sketch, "E4.0.13.11", {"center": v(76.2, 50.8) * mm, "radius": 3.18 * mm});
            skCircle(sketch, "E4.0.13.12", {"center": v(76.2, 38.1) * mm, "radius": 3.18 * mm});
            skCircle(sketch, "E4.0.13.13", {"center": v(76.2, 25.4) * mm, "radius": 3.18 * mm});
            skCircle(sketch, "E4.0.13.14", {"center": v(76.2, 12.7) * mm, "radius": 3.18 * mm});
            skCircle(sketch, "E4.0.13.15", {"center": v(76.2, 0) * mm, "radius": 3.18 * mm});
            skCircle(sketch, "E4.0.13.16", {"center": v(76.2, -12.7) * mm, "radius": 3.18 * mm});
            skCircle(sketch, "E4.0.13.17", {"center": v(76.2, -25.4) * mm, "radius": 3.18 * mm});
            skCircle(sketch, "E4.0.13.18", {"center": v(76.2, -38.1) * mm, "radius": 3.18 * mm});
            skCircle(sketch, "E4.0.13.19", {"center": v(76.2, -50.8) * mm, "radius": 3.18 * mm});
            skCircle(sketch, "E4.0.13.20", {"center": v(76.2, -63.5) * mm, "radius": 3.18 * mm});
            skCircle(sketch, "E4.0.13.21", {"center": v(76.2, -76.2) * mm, "radius": 3.18 * mm});
            skCircle(sketch, "E4.0.13.22", {"center": v(76.2, -88.9) * mm, "radius": 3.18 * mm});
            skCircle(sketch, "E4.0.13.23", {"center": v(76.2, -101.6) * mm, "radius": 3.18 * mm});
            skCircle(sketch, "E4.0.13.24", {"center": v(76.2, -114.3) * mm, "radius": 3.18 * mm});
            skCircle(sketch, "E4.0.13.25", {"center": v(76.2, -127) * mm, "radius": 3.18 * mm});
            skCircle(sketch, "E4.0.13.26", {"center": v(76.2, -139.7) * mm, "radius": 3.18 * mm});
            skCircle(sketch, "E4.0.13.27", {"center": v(76.2, -152.4) * mm, "radius": 3.18 * mm});
            skCircle(sketch, "E4.0.13.28", {"center": v(76.2, -165.1) * mm, "radius": 3.18 * mm});
            skCircle(sketch, "E4.0.13.29", {"center": v(76.2, -177.8) * mm, "radius": 3.18 * mm});
            skCircle(sketch, "E5.0.14.0", {"center": v(88.9, 190.5) * mm, "radius": 3.18 * mm});
            skCircle(sketch, "E5.0.14.1", {"center": v(88.9, 177.8) * mm, "radius": 3.18 * mm});
            skCircle(sketch, "E5.0.14.2", {"center": v(88.9, 165.1) * mm, "radius": 3.18 * mm});
            skCircle(sketch, "E5.0.14.3", {"center": v(88.9, 152.4) * mm, "radius": 3.18 * mm});
            skCircle(sketch, "E5.0.14.4", {"center": v(88.9, 139.7) * mm, "radius": 3.18 * mm});
            skCircle(sketch, "E5.0.14.5", {"center": v(88.9, 127) * mm, "radius": 3.18 * mm});
            skCircle(sketch, "E5.0.14.6", {"center": v(88.9, 114.3) * mm, "radius": 3.18 * mm});
            skCircle(sketch, "E5.0.14.7", {"center": v(88.9, 101.6) * mm, "radius": 3.18 * mm});
            skCircle(sketch, "E5.0.14.8", {"center": v(88.9, 88.9) * mm, "radius": 3.18 * mm});
            skCircle(sketch, "E5.0.14.9", {"center": v(88.9, 76.2) * mm, "radius": 3.18 * mm});
            skCircle(sketch, "E5.0.14.10", {"center": v(88.9, 63.5) * mm, "radius": 3.18 * mm});
            skCircle(sketch, "E5.0.14.11", {"center": v(88.9, 50.8) * mm, "radius": 3.18 * mm});
            skCircle(sketch, "E5.0.14.12", {"center": v(88.9, 38.1) * mm, "radius": 3.18 * mm});
            skCircle(sketch, "E5.0.14.13", {"center": v(88.9, 25.4) * mm, "radius": 3.18 * mm});
            skCircle(sketch, "E5.0.14.14", {"center": v(88.9, 12.7) * mm, "radius": 3.18 * mm});
            skCircle(sketch, "E5.0.14.15", {"center": v(88.9, 0) * mm, "radius": 3.18 * mm});
            skCircle(sketch, "E5.0.14.16", {"center": v(88.9, -12.7) * mm, "radius": 3.18 * mm});
            skCircle(sketch, "E5.0.14.17", {"center": v(88.9, -25.4) * mm, "radius": 3.18 * mm});
            skCircle(sketch, "E5.0.14.18", {"center": v(88.9, -38.1) * mm, "radius": 3.18 * mm});
            skCircle(sketch, "E5.0.14.19", {"center": v(88.9, -50.8) * mm, "radius": 3.18 * mm});
            skCircle(sketch, "E5.0.14.20", {"center": v(88.9, -63.5) * mm, "radius": 3.18 * mm});
            skCircle(sketch, "E5.0.14.21", {"center": v(88.9, -76.2) * mm, "radius": 3.18 * mm});
            skCircle(sketch, "E5.0.14.22", {"center": v(88.9, -88.9) * mm, "radius": 3.18 * mm});
            skCircle(sketch, "E5.0.14.23", {"center": v(88.9, -101.6) * mm, "radius": 3.18 * mm});
            skCircle(sketch, "E5.0.14.24", {"center": v(88.9, -114.3) * mm, "radius": 3.18 * mm});
            skCircle(sketch, "E5.0.14.25", {"center": v(88.9, -127) * mm, "radius": 3.18 * mm});
            skCircle(sketch, "E5.0.14.26", {"center": v(88.9, -139.7) * mm, "radius": 3.18 * mm});
            skCircle(sketch, "E5.0.14.27", {"center": v(88.9, -152.4) * mm, "radius": 3.18 * mm});
            skCircle(sketch, "E5.0.14.28", {"center": v(88.9, -165.1) * mm, "radius": 3.18 * mm});
            skCircle(sketch, "E5.0.14.29", {"center": v(88.9, -177.8) * mm, "radius": 3.18 * mm});
            skCircle(sketch, "E6.0.0.30", {"center": v(-88.9, -190.5) * mm, "radius": 3.18 * mm});
            skCircle(sketch, "E6.0.1.30", {"center": v(-76.2, -190.5) * mm, "radius": 3.18 * mm});
            skCircle(sketch, "E6.0.2.30", {"center": v(-63.5, -190.5) * mm, "radius": 3.18 * mm});
            skCircle(sketch, "E6.0.3.30", {"center": v(-50.8, -190.5) * mm, "radius": 3.18 * mm});
            skCircle(sketch, "E6.0.4.30", {"center": v(-38.1, -190.5) * mm, "radius": 3.18 * mm});
            skCircle(sketch, "E6.0.5.30", {"center": v(-25.4, -190.5) * mm, "radius": 3.18 * mm});
            skCircle(sketch, "E6.0.6.30", {"center": v(-12.7, -190.5) * mm, "radius": 3.18 * mm});
            skCircle(sketch, "E6.0.7.30", {"center": v(0, -190.5) * mm, "radius": 3.18 * mm});
            skCircle(sketch, "E6.0.8.30", {"center": v(12.7, -190.5) * mm, "radius": 3.18 * mm});
            skCircle(sketch, "E6.0.9.30", {"center": v(25.4, -190.5) * mm, "radius": 3.18 * mm});
            skCircle(sketch, "E6.0.10.30", {"center": v(38.1, -190.5) * mm, "radius": 3.18 * mm});
            skCircle(sketch, "E6.0.11.30", {"center": v(50.8, -190.5) * mm, "radius": 3.18 * mm});
            skCircle(sketch, "E6.0.12.30", {"center": v(63.5, -190.5) * mm, "radius": 3.18 * mm});
            skCircle(sketch, "E6.0.13.30", {"center": v(76.2, -190.5) * mm, "radius": 3.18 * mm});
            skCircle(sketch, "E6.0.14.30", {"center": v(88.9, -190.5) * mm, "radius": 3.18 * mm});
            skSolve(sketch);
        }
        {
            var Q0;
            Q0 = qSketchRegion(id + "F2", true);
            extrude(context, id + "F3", {"entities" : qUnion([Q0]), "operationType" : NewBodyOperationType.REMOVE, "endBound" : BoundingType.THROUGH_ALL, "oppositeDirection" : true, "depth" : 25.4 * mm});
        }
    });
